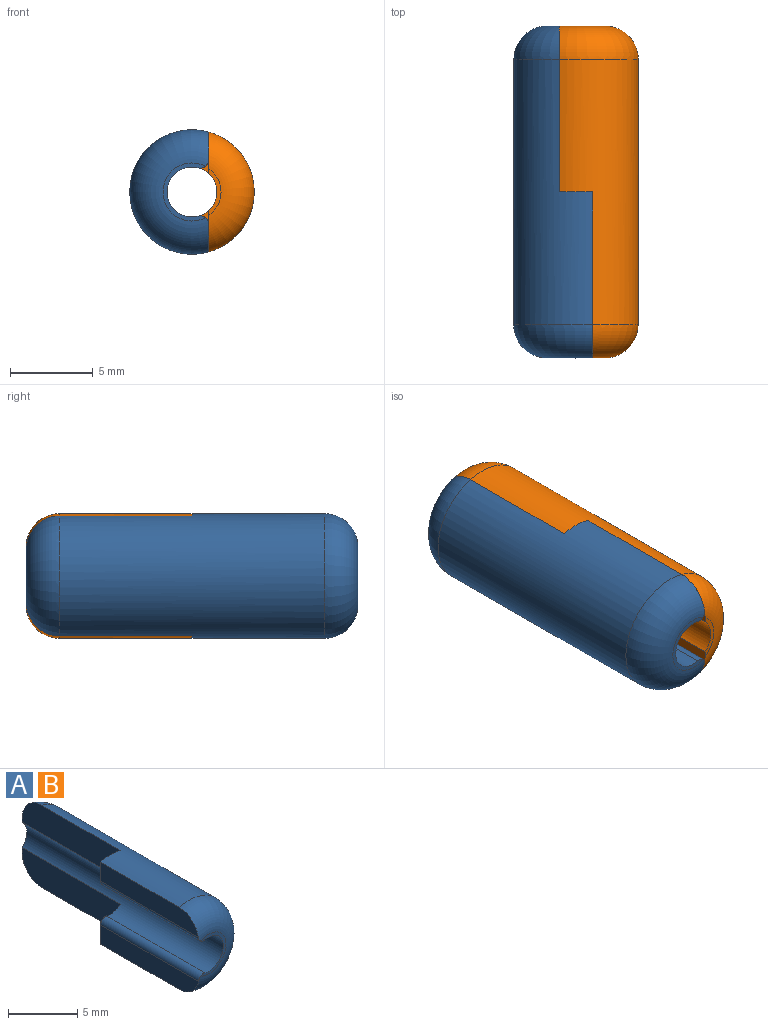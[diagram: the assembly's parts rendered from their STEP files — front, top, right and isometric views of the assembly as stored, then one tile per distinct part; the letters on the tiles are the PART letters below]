
ASSEMBLY  parts=2 mates=1
PART A: 14 faces, bbox 5.6x20x7.5 mm
  f0: cylinder r=1.5mm len=20mm, axis (0,1,0), area 79.9mm2, adj f1,f3,f6,f7,f8,f9,f12,f13
  f1: plane 3.5x2.57mm, normal (0,-1,0), area 1.6mm2, adj f0,f11,f12,f13
  f2: cylinder r=3.75mm len=16mm, axis (0,1,0), area 188.5mm2, adj f4,f5,f6,f7,f8,f9,f10,f11
  f3: plane 2.87x0.75mm, normal (0,1,0), area 0.7mm2, adj f0,f7,f9,f10
  f4: plane 9.95x1.68mm, normal (-1,0,0), area 15.9mm2, adj f2,f8,f11,f12
  f5: plane 9.96x1.68mm, normal (-1,0,0), area 15.9mm2, adj f2,f6,f11,f13
  f6: plane 2.63x2mm, normal (0,1,0), area 4.5mm2, adj f0,f2,f5,f7,f13
  f7: plane 10x2.5mm, normal (-1,0,0), area 24.1mm2, adj f0,f2,f3,f6,f10
  f8: plane 2.63x2mm, normal (0,1,0), area 4.5mm2, adj f0,f2,f4,f9,f12
  f9: plane 10x2.5mm, normal (-1,0,0), area 24.1mm2, adj f0,f2,f3,f8,f10
  f10: torus R=1.75mm, axis (0,-1,0), area 23.4mm2, adj f2,f3,f7,f9
  f11: torus R=1.75mm, axis (0,-1,0), area 36.2mm2, adj f1,f2,f4,f5,f12,f13
  f12: cylinder r=0.5mm len=10mm, axis (0,1,0), area 9.1mm2, adj f0,f1,f4,f8,f11
  f13: cylinder r=0.5mm len=10mm, axis (0,1,0), area 9.1mm2, adj f0,f1,f5,f6,f11
PART B: same geometry as A
PLACE A rot(axis=(0,-1,0),180deg) t=(-8.39,4.85,-3.21)mm
PLACE B rot(axis=(-1,0,0),180deg) t=(-8.39,-15.15,-3.21)mm
MATE revolute B.f2 <-> A.f2  axis (0,-1,0) through (-8.39,-5.15,-3.21)mm
